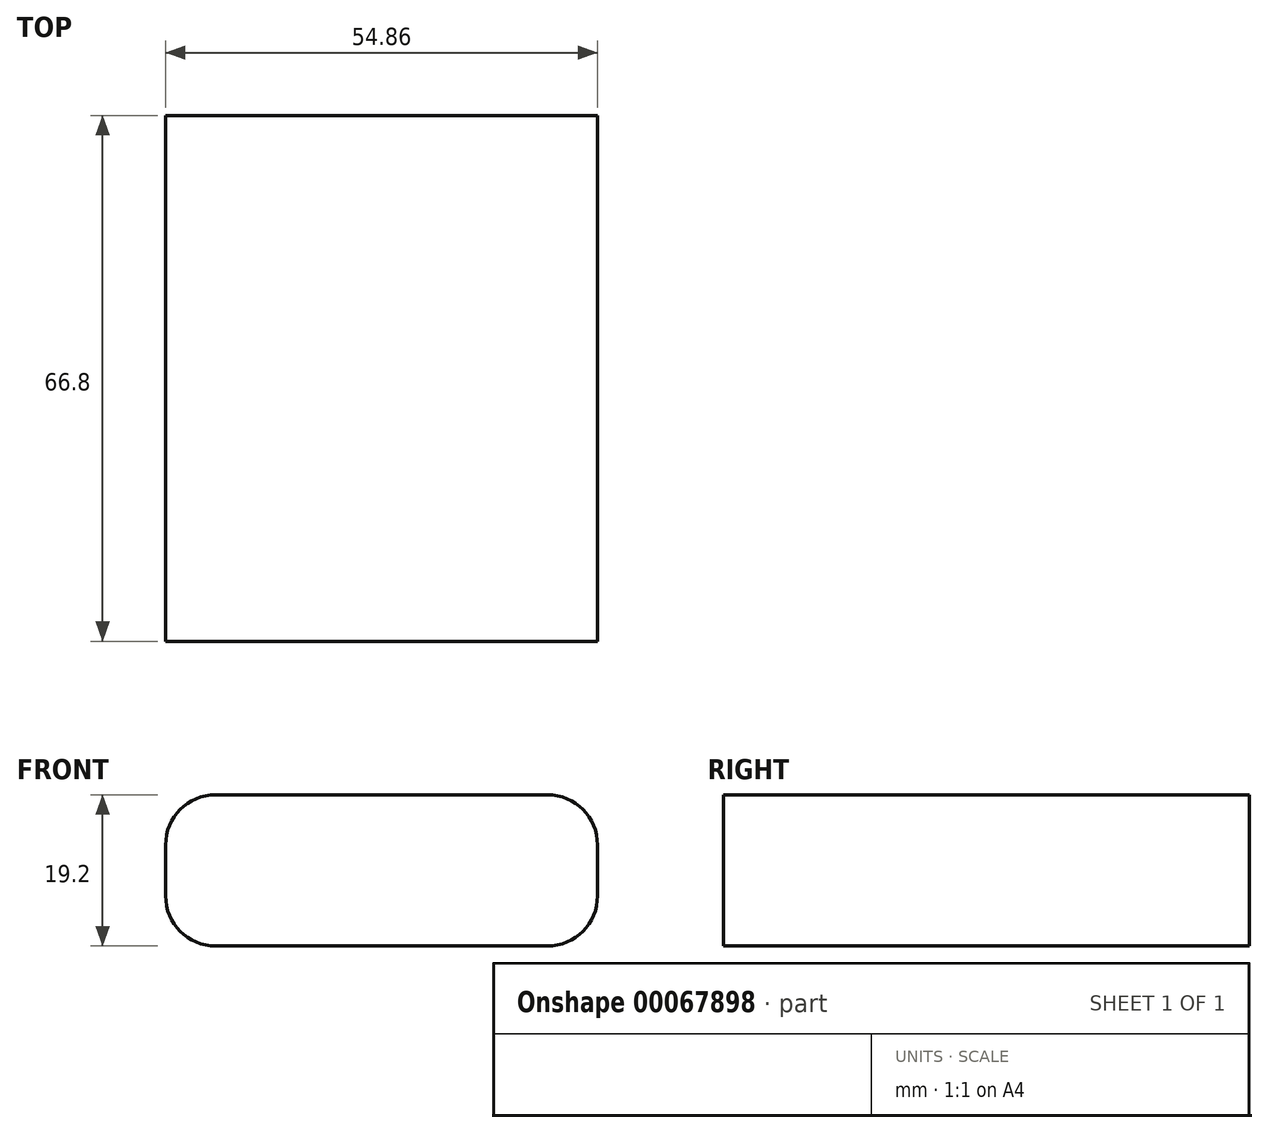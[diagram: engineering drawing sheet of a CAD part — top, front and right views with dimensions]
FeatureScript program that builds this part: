
annotation { "Feature Type Name" : "Feature", "Feature Type Description" : "" }
export const myFeature = defineFeature(function(context is Context, id is Id, definition is map)
    precondition{}
    {
        {
            var Q0;
            Q0=qCreatedBy(makeId("Top.planeOp"),FACE);
            var sketch = newSketch(context, id + "F0", { "sketchPlane" : qUnion([Q0])});
            skLineSegment(sketch, "E0.bottom", {"start": v(27.43, 33.4) * mm, "end": v(-27.43, 33.4) * mm});
            skLineSegment(sketch, "E0.top", {"start": v(27.43, -33.4) * mm, "end": v(-27.43, -33.4) * mm});
            skLineSegment(sketch, "E0.left", {"start": v(27.43, 33.4) * mm, "end": v(27.43, -33.4) * mm});
            skLineSegment(sketch, "E0.right", {"start": v(-27.43, 33.4) * mm, "end": v(-27.43, -33.4) * mm});
            skPoint(sketch, "E0.middle", {"position": v(0, 0) * mm});
            skSolve(sketch);
        }
        {
            var Q0;
            Q0 = qSketchRegion(id + "F0", true);
            extrude(context, id + "F1", {"entities" : qUnion([Q0]), "depth" : 19.2 * mm});
        }
        {
            var Q0;
            Q0=makeQuery(id+"F1.opExtrude","CAP_EDGE",EDGE,{"disambiguationData":[OSD([sQuery(id+"F0.wireOp",EDGE,"E0.left")])],"isStart":false});
            var Q1;
            Q1=makeQuery(id+"F1.opExtrude","CAP_EDGE",EDGE,{"disambiguationData":[OSD([sQuery(id+"F0.wireOp",EDGE,"E0.left")])],"isStart":true});
            var Q2;
            Q2=makeQuery(id+"F1.opExtrude","CAP_EDGE",EDGE,{"disambiguationData":[OSD([sQuery(id+"F0.wireOp",EDGE,"E0.right")])],"isStart":false});
            var Q3;
            Q3=makeQuery(id+"F1.opExtrude","CAP_EDGE",EDGE,{"disambiguationData":[OSD([sQuery(id+"F0.wireOp",EDGE,"E0.right")])],"isStart":true});
            fillet(context, id + "F2", {"entities" : qUnion([Q0, Q1, Q2, Q3]), "radius" : 6.35 * mm, "tangentPropagation" : true, "allowEdgeOverflow" : false});
        }
    });
